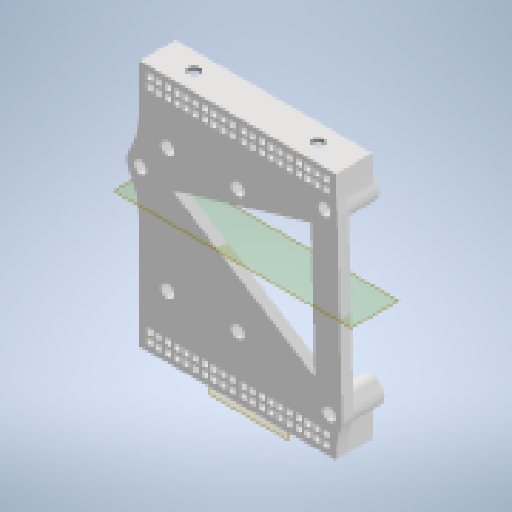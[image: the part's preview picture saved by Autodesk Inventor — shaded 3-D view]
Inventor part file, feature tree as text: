
AUTODESK INVENTOR PART (.ipt)
format: ipt  version: 2024.2 (Build 282272000, 272)  size: 968,704 bytes
history: native  units: mm
features: other x10, sketch x8, extrude x8, thread x8, reference x7, plane x6, projected_geometry x4, fillet x2, mirror x1
ambient origin geometry x8: Origin, YZ Plane, XZ Plane, XY Plane, X Axis, Y Axis, Z Axis, Center Point
bodies: Body1 (feature_tree)
feature tree (54):
  sketch  "Sketch1"  dims[d0=1.2mm d3=1.2mm]
  plane  "Work Plane1"
  extrude  "Extrusion4"  Depth=1.2mm
  extrude  "Extrusion5"  Depth=1.0mm
  extrude  "Extrusion6"  Depth=3.0mm TaperAngle=0.0deg
  fillet  "Fillet1"  Radius=7.5mm
  sketch  "Sketch7"  dims[d15=7.5mm d16=7.5mm]
  plane  "Work Plane2"
  extrude  "Extrusion7"  Depth=7.5mm
  extrude  "Extrusion8"  Depth=27.0mm
  extrude  "Extrusion9"  Depth=7.0mm
  thread  "Thread1"  [1 undecoded]
  thread  "Thread2"  [1 undecoded]
  thread  "Thread3"  [1 undecoded]
  thread  "Thread4"  [1 undecoded]
  thread  "Thread5"  [1 undecoded]
  thread  "Thread6"  [1 undecoded]
  thread  "Thread7"  [1 undecoded]
  thread  "Thread8"  [1 undecoded]
  plane  "Work Plane3"
  sketch  "Sketch10"  dims[d32=10.0mm d33=3.2mm]
  plane  "Work Plane4"
  extrude  "Extrusion10"  Depth=10.0mm
  plane  "Work Plane5"
  extrude  "Extrusion11"  TaperAngle=0.0deg  [1 undecoded]
  fillet  "Fillet2"  Radius=1.0mm
  mirror  "Mirror1"
  sketch  "Sketch5"  dims[d8=1.0mm d9=1.0mm]
  reference  "Reference9"
  reference  "Reference10"
  reference  "Reference11"
  reference  "Reference12"
  projected_geometry  "Projected Loop1"
  projected_geometry  "Projected Loop2"
  sketch  "Sketch6"  dims[d10=7.0mm d11=0.0mm d12=3.0mm d13=0.0mm d14=7.5mm]
  reference  "Reference13"
  reference  "Reference14"
  reference  "Reference15"
  projected_geometry  "Projected Loop3"
  projected_geometry  "Projected Loop4"
  sketch  "Sketch8"  dims[d17=3.0mm d18=0.0mm d19=27.0mm]
  sketch  "Sketch9"  dims[d20=7.0mm d21=7.0mm d22=7.0mm d23=3.0mm d24=0.0mm d25=3.5mm d26=3.5mm d27=3.5mm d28=3.5mm d29=10.0mm d30=0.0mm d31=3.2mm]
  sketch  "Sketch11"  dims[d34=10.0mm d35=0.0mm d36=0.0mm d37=1.0mm d38=0.0mm d39=1.0mm d40=0.0mm d41=1.0mm d42=0.0mm d43=1.0mm d44=0.0mm d45=1.0mm d46=0.0mm d47=1.0mm d48=0.0mm d49=1.0mm d50=0.0mm d51=1.0mm d52=0.0mm d53=10.0mm d54=10.0mm d55=0.0mm d56=20.0mm d57=3.2mm d60=10.0mm d61=3.2mm d62=5.0mm d63=7.5mm d64=3.0mm d65=0.0mm d66=3.75mm d1=0.5mm d2=0.872665mm d4=0.872665mm]
  plane  "Work Plane6"
  other  "<userpath>\Desktop\meca_robotbebou\iks01A2\iks01A2switch.iam"
  other  "iks01A2switch.iam"
  other  "zl262-20d_p2-54_l25-9_w5_h8-5:2"
  other  "zl262-20d_p2-54_l25-9_w5_h8-5:1"
  other  "zl262-20d_p2-54_l25-9_w5_h8-5:4"
  other  "zl262-20d_p2-54_l25-9_w5_h8-5:3"
  other  "NUCLEO-F411RE:1"
  other  "<userpath>\Desktop\meca_robotbebou\Robotbebou.iam"
  other  "Robotbebou.iam"
  other  "profile259:1"
note: 9 required parameter values undecoded (feature->parameter linkage not recoverable at this tier; creation-order binding heuristic only, values carry confidence <= 0.55)
